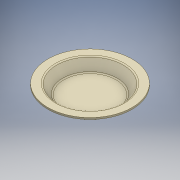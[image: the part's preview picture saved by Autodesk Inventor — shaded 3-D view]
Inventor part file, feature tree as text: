
AUTODESK INVENTOR PART (.ipt)
format: ipt  version: 2016 (Build 200138000, 138)  size: 165,376 bytes
history: native  units: mm
features: other x3, revolve x1, sketch x1
ambient origin geometry x8: Origin, YZ Plane, XZ Plane, XY Plane, X Axis, Y Axis, Z Axis, Center Point
bodies: Body1 (feature_tree)
feature tree (5):
  other  "Sólido1"
  revolve  "Revolución1"  [1 undecoded]
  other  "Desplazar cuerpo1"
  other  "Desplazar cuerpo2"
  sketch  "Boceto3"  dims[d6=125.0mm d8=80.0mm d9=5.0mm d10=5.0mm d12=100.0mm d13=85.0mm d16=5.0mm d17=5.0mm d18=90.0deg d19=90.0deg d20=10.0mm d21=0.0mm d22=0.0mm]
note: 1 required parameter value undecoded (feature->parameter linkage not recoverable at this tier; creation-order binding heuristic only, values carry confidence <= 0.55)
